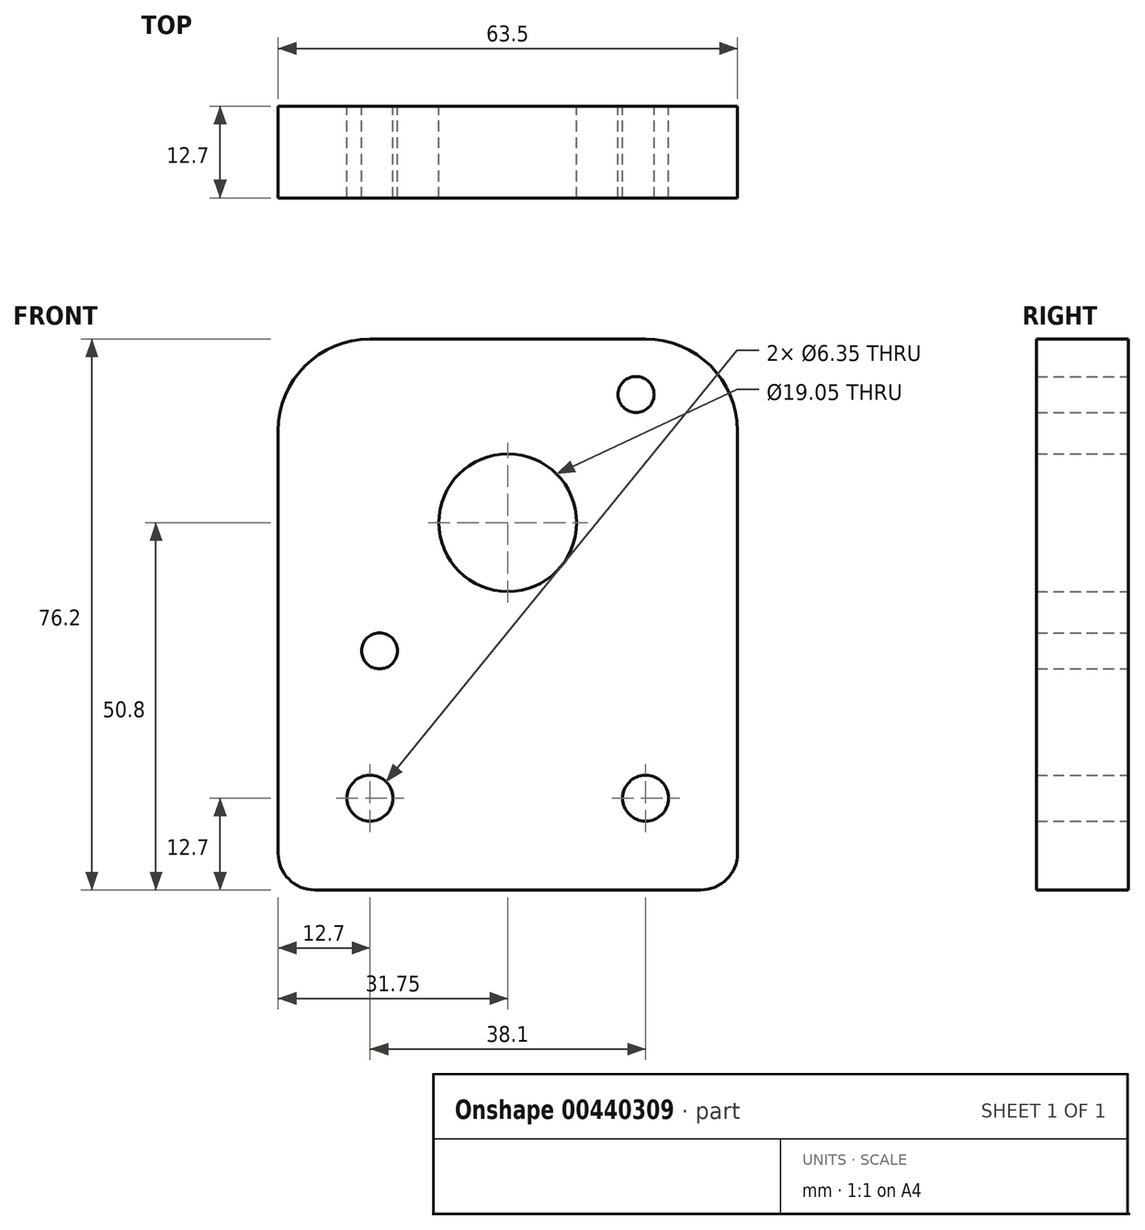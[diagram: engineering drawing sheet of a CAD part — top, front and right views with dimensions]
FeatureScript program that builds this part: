
annotation { "Feature Type Name" : "Feature", "Feature Type Description" : "" }
export const myFeature = defineFeature(function(context is Context, id is Id, definition is map)
    precondition{}
    {
        {
            var Q0;
            Q0=qCreatedBy(makeId("Front.planeOp"),FACE);
            var sketch = newSketch(context, id + "F0", { "sketchPlane" : qUnion([Q0])});
            skLineSegment(sketch, "E0.bottom", {"start": v(31.75, -25.4) * mm, "end": v(-31.75, -25.4) * mm});
            skLineSegment(sketch, "E0.top", {"start": v(19.05, 50.8) * mm, "end": v(-19.05, 50.8) * mm});
            skLineSegment(sketch, "E0.left", {"start": v(31.75, -25.4) * mm, "end": v(31.75, 38.1) * mm});
            skLineSegment(sketch, "E0.right", {"start": v(-31.75, -25.4) * mm, "end": v(-31.75, 38.1) * mm});
            skLineSegment(sketch, "E1", {"start": v(-31.75, 0) * mm, "end": v(31.75, 0) * mm, "construction": true});
            skLineSegment(sketch, "E2", {"start": v(-31.75, -12.7) * mm, "end": v(31.75, -12.7) * mm, "construction": true});
            skCircle(sketch, "E3", {"center": v(-19.05, -12.7) * mm, "radius": 3.18 * mm});
            skLineSegment(sketch, "E4", {"start": v(0, 0) * mm, "end": v(0, -25.4) * mm, "construction": true});
            skCircle(sketch, "E5.MirrorC", {"center": v(19.05, -12.7) * mm, "radius": 3.18 * mm});
            skLineSegment(sketch, "E6", {"start": v(0, 0) * mm, "end": v(0, 50.8) * mm, "construction": true});
            skCircle(sketch, "E7", {"center": v(0, 25.4) * mm, "radius": 9.53 * mm});
            skLineSegment(sketch, "E8.bottom", {"start": v(-17.73, 43.13) * mm, "end": v(17.73, 43.13) * mm, "construction": true});
            skLineSegment(sketch, "E8.top", {"start": v(-17.73, 7.67) * mm, "end": v(17.73, 7.67) * mm, "construction": true});
            skLineSegment(sketch, "E8.left", {"start": v(-17.73, 43.13) * mm, "end": v(-17.73, 7.67) * mm, "construction": true});
            skLineSegment(sketch, "E8.right", {"start": v(17.73, 43.13) * mm, "end": v(17.73, 7.67) * mm, "construction": true});
            skCircle(sketch, "E9", {"center": v(17.73, 43.13) * mm, "radius": 2.49 * mm});
            skCircle(sketch, "E10", {"center": v(-17.73, 7.67) * mm, "radius": 2.49 * mm});
            skPoint(sketch, "E11.visualSharp", {"position": v(-31.75, 50.8) * mm});
            skArc(sketch, "E11.filletArc", {"start": v(-19.05, 50.8) * mm, "mid": v(-28.03, 47.08) * mm, "end": v(-31.75, 38.1) * mm});
            skPoint(sketch, "E12.visualSharp", {"position": v(31.75, 50.8) * mm});
            skArc(sketch, "E12.filletArc", {"start": v(31.75, 38.1) * mm, "mid": v(28.03, 47.08) * mm, "end": v(19.05, 50.8) * mm});
            skSolve(sketch);
        }
        {
            var Q0;
            Q0=makeQuery(id+"F0.imprint","IMPRINT",FACE,{"disambiguationData":[TD([[makeQuery(id+"F0.imprint","IMPRINT",EDGE,{"derivedFrom":sQuery(id+"F0.wireOp",EDGE,"E0.bottom")}),-1.0]])]});
            extrude(context, id + "F1", {"entities" : qUnion([Q0]), "depth" : 12.7 * mm});
        }
        {
            var Q0;
            Q0=makeQuery(id+"F1.opExtrude","SWEPT_EDGE",EDGE,{"disambiguationData":[OSD([sQuery(id+"F0.wireOp",EDGE,"E0.top"),sQuery(id+"F0.wireOp",EDGE,"E0.right")])]});
            var Q1;
            Q1=makeQuery(id+"F1.opExtrude","SWEPT_EDGE",EDGE,{"disambiguationData":[OSD([sQuery(id+"F0.wireOp",EDGE,"E0.top"),sQuery(id+"F0.wireOp",EDGE,"E0.left")])]});
            var Q2;
            Q2=makeQuery(id+"F1.opExtrude","SWEPT_EDGE",EDGE,{"disambiguationData":[OSD([sQuery(id+"F0.wireOp",EDGE,"E0.bottom"),sQuery(id+"F0.wireOp",EDGE,"E0.left")])]});
            var Q3;
            Q3=makeQuery(id+"F1.opExtrude","SWEPT_EDGE",EDGE,{"disambiguationData":[OSD([sQuery(id+"F0.wireOp",EDGE,"E0.bottom"),sQuery(id+"F0.wireOp",EDGE,"E0.right")])]});
            fillet(context, id + "F2", {"entities" : qUnion([Q0, Q1, Q2, Q3]), "radius" : 5.08 * mm, "tangentPropagation" : true, "allowEdgeOverflow" : false});
        }
    });
